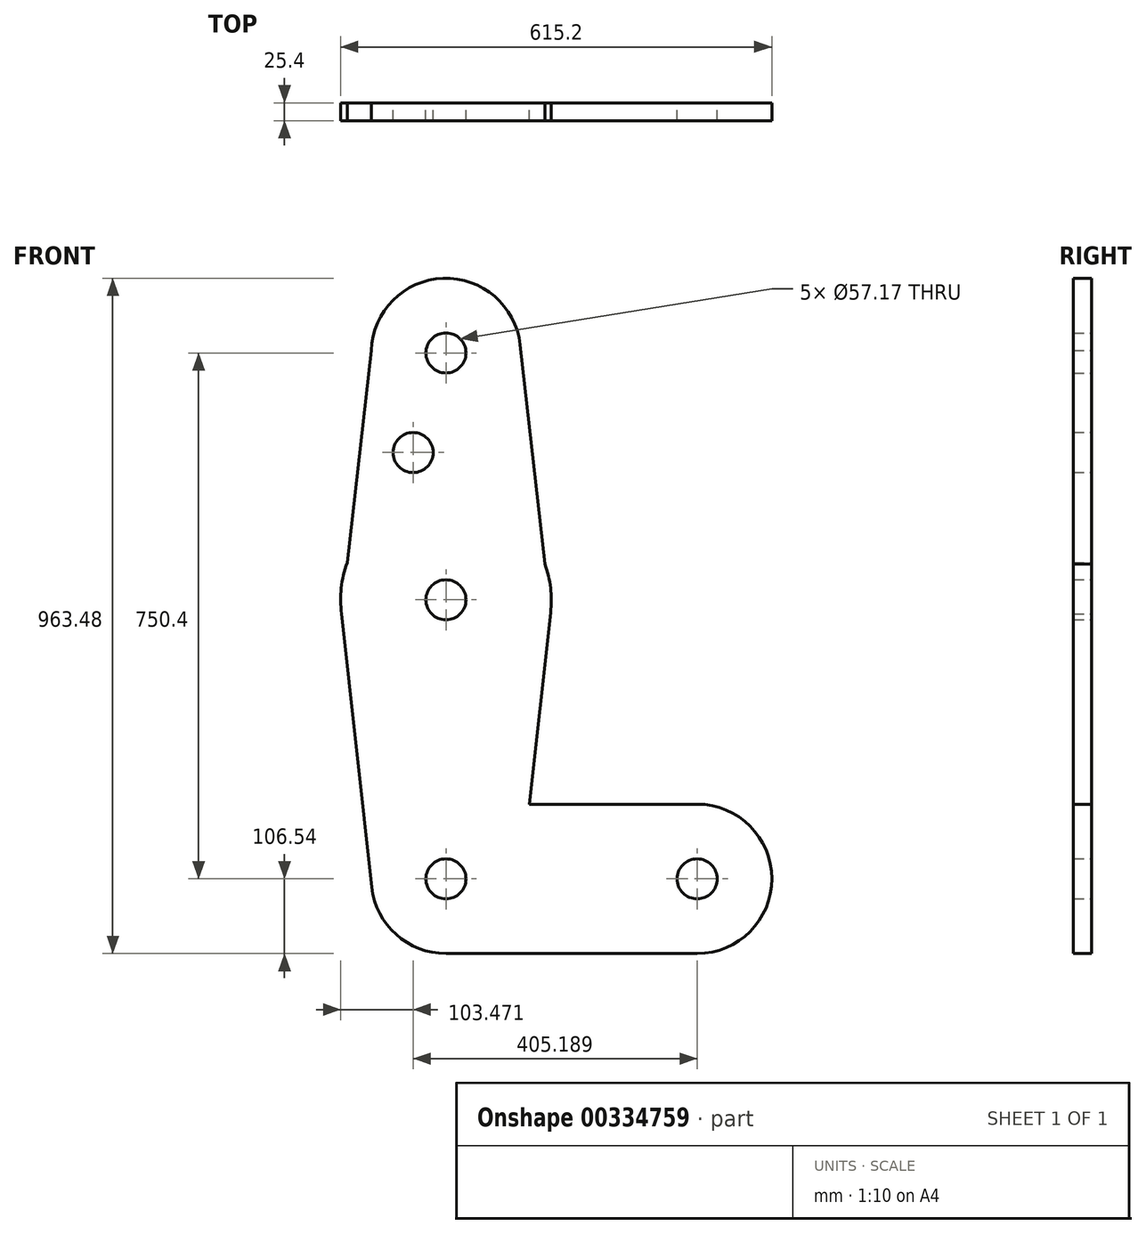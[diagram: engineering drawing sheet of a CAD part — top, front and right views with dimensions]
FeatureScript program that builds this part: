
annotation { "Feature Type Name" : "Feature", "Feature Type Description" : "" }
export const myFeature = defineFeature(function(context is Context, id is Id, definition is map)
    precondition{}
    {
        {
            var Q0;
            Q0=qCreatedBy(makeId("Front.planeOp"),FACE);
            var sketch = newSketch(context, id + "F0", { "sketchPlane" : qUnion([Q0])});
            skLineSegment(sketch, "E0", {"start": v(0, 0) * mm, "end": v(0, 391.28) * mm});
            skLineSegment(sketch, "E1", {"start": v(0, 391.28) * mm, "end": v(0, -359.12) * mm});
            skLineSegment(sketch, "E2", {"start": v(0, -359.12) * mm, "end": v(358.4, -359.12) * mm});
            skCircle(sketch, "E3", {"center": v(0, -359.12) * mm, "radius": 106.54 * mm});
            skCircle(sketch, "E4", {"center": v(358.4, -359.12) * mm, "radius": 106.54 * mm});
            skCircle(sketch, "E5", {"center": v(0, 391.28) * mm, "radius": 106.54 * mm});
            skCircle(sketch, "E6", {"center": v(0, 39.07) * mm, "radius": 150.26 * mm});
            skLineSegment(sketch, "E7", {"start": v(-104.6, 411.48) * mm, "end": v(-148.93, 19.12) * mm});
            skLineSegment(sketch, "E8", {"start": v(-148.93, 19.12) * mm, "end": v(-105.9, -370.8) * mm});
            skLineSegment(sketch, "E9", {"start": v(105.88, 403.1) * mm, "end": v(149.19, 21.13) * mm});
            skLineSegment(sketch, "E10", {"start": v(149.19, 21.13) * mm, "end": v(107.19, -359.12) * mm});
            skLineSegment(sketch, "E11", {"start": v(0, -252.58) * mm, "end": v(358.4, -252.58) * mm});
            skLineSegment(sketch, "E12", {"start": v(0, -465.66) * mm, "end": v(358.4, -465.66) * mm});
            skCircle(sketch, "E13", {"center": v(0, 391.28) * mm, "radius": 28.58 * mm});
            skCircle(sketch, "E14", {"center": v(-46.79, 249.15) * mm, "radius": 28.58 * mm});
            skCircle(sketch, "E15", {"center": v(0, 39.07) * mm, "radius": 28.58 * mm});
            skCircle(sketch, "E16", {"center": v(0, -359.12) * mm, "radius": 28.58 * mm});
            skCircle(sketch, "E17", {"center": v(358.4, -359.12) * mm, "radius": 28.58 * mm});
            skSolve(sketch);
        }
        {
            var Q0;
            Q0 = qSketchRegion(id + "F0", true);
            var Q1;
            {var subQ3=sQuery(id+"F0.wireOp",EDGE,"E16");var subQ5=sQuery(id+"F0.wireOp",EDGE,"E2");var subQ6=makeQuery(id+"F0.imprint","INTERSECT",VERTEX,{"derivedFrom":[subQ5,subQ3]});Q1=makeQuery(id+"F0.imprint","IMPRINT",FACE,{"disambiguationData":[TD([[makeQuery(id+"F0.imprint","IMPRINT",EDGE,{"disambiguationData":[TD([[subQ6,-1.0]])],"derivedFrom":subQ5}),1.0]])]});}
            extrude(context, id + "F1", {"entities" : qUnion([Q0, Q1]), "depth" : 25.4 * mm});
        }
    });
